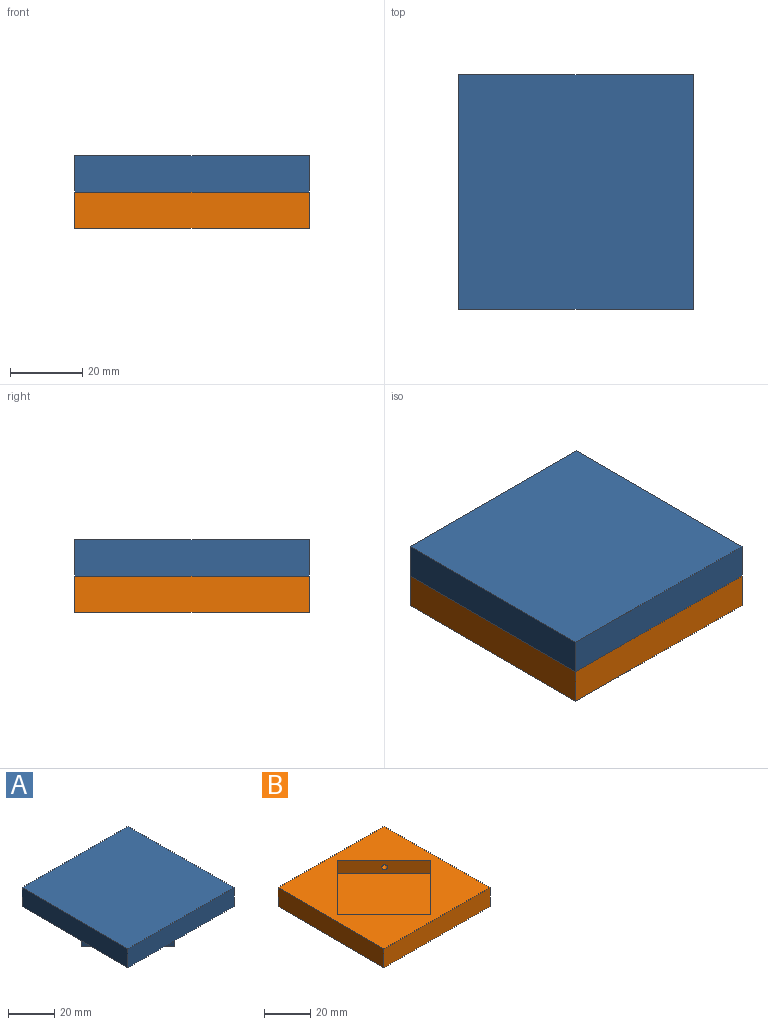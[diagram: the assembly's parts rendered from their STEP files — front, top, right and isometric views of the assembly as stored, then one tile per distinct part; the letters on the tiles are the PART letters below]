
ASSEMBLY  parts=2 mates=1
PART A: 24 faces, bbox 65x65x16.9 mm
  f0: cylinder r=1.25mm len=3.89mm, axis (0.71,0.71,0), area 23.6mm2, adj f1,f15
  f1: plane 2.5x1.77mm, normal (0.71,0.71,0), area 4.9mm2, adj f0
  f2: cylinder r=1.25mm len=3.89mm, axis (-0.71,0.71,0), area 23.6mm2, adj f3,f14
  f3: plane 2.5x1.77mm, normal (-0.71,0.71,0), area 4.9mm2, adj f2
  f4: cylinder r=1.25mm len=3.89mm, axis (-0.71,-0.71,0), area 23.6mm2, adj f5,f13
  f5: plane 2.5x1.77mm, normal (-0.71,-0.71,0), area 4.9mm2, adj f4
  f6: plane 56.57x56.57mm, normal (0,0,-1), area 576mm2, adj f13,f14,f15,f16,f17,f18,f19,f20
  f7: plane 65x10mm, normal (0,1,0), area 650mm2, adj f8,f10,f11,f12
  f8: plane 65x10mm, normal (1,0,0), area 650mm2, adj f7,f9,f11,f12
  f9: plane 65x10mm, normal (0,-1,0), area 650mm2, adj f8,f10,f11,f12
  f10: plane 65x10mm, normal (-1,0,0), area 650mm2, adj f7,f9,f11,f12
  f11: plane 65x65mm, normal (0,0,-1), area 2625mm2, adj f7,f8,f9,f10,f13,f14,f15,f16
  f12: plane 65x65mm, normal (0,0,1), area 4225mm2, adj f7,f8,f9,f10
  f13: plane 28.28x28.28mm, normal (-0.71,-0.71,0), area 271.1mm2, adj f4,f6,f11,f14,f16
  f14: plane 28.28x28.28mm, normal (-0.71,0.71,0), area 271.1mm2, adj f2,f6,f11,f13,f15
  f15: plane 28.28x28.28mm, normal (0.71,0.71,0), area 271.1mm2, adj f0,f6,f11,f14,f16
  f16: plane 28.28x28.28mm, normal (0.71,-0.71,0), area 271.1mm2, adj f6,f11,f13,f15,f22
  f17: plane 22.63x22.63mm, normal (-0.71,0.71,0), area 448mm2, adj f6,f18,f20,f21
  f18: plane 22.63x22.63mm, normal (0.71,0.71,0), area 448mm2, adj f6,f17,f19,f21
  f19: plane 22.63x22.63mm, normal (0.71,-0.71,0), area 448mm2, adj f6,f18,f20,f21
  f20: plane 22.63x22.63mm, normal (-0.71,-0.71,0), area 448mm2, adj f6,f17,f19,f21
  f21: plane 45.26x45.26mm, normal (0,0,-1), area 1024mm2, adj f17,f18,f19,f20
  f22: cylinder r=1.25mm len=3.89mm, axis (0.71,-0.71,0), area 23.6mm2, adj f16,f23
  f23: plane 2.5x1.77mm, normal (0.71,-0.71,0), area 4.9mm2, adj f22
PART B: 19 faces, bbox 65x65x10 mm
  f0: cylinder r=1.25mm len=6.72mm, axis (-0.71,0.71,0), area 55mm2, adj f1,f14
  f1: plane 2.5x1.77mm, normal (-0.71,0.71,0), area 4.9mm2, adj f0
  f2: cylinder r=1.25mm len=6.72mm, axis (-0.71,-0.71,0), area 55mm2, adj f3,f15
  f3: plane 2.5x1.77mm, normal (-0.71,-0.71,0), area 4.9mm2, adj f2
  f4: cylinder r=1.25mm len=6.72mm, axis (0.71,-0.71,0), area 55mm2, adj f5,f12
  f5: plane 2.5x1.77mm, normal (0.71,-0.71,0), area 4.9mm2, adj f4
  f6: plane 65x65mm, normal (0,0,1), area 2576.6mm2, adj f7,f8,f9,f10,f12,f13,f14,f15
  f7: plane 65x10mm, normal (0,1,0), area 650mm2, adj f6,f8,f10,f11
  f8: plane 65x10mm, normal (-1,0,0), area 650mm2, adj f6,f7,f9,f11
  f9: plane 65x10mm, normal (0,-1,0), area 650mm2, adj f6,f8,f10,f11
  f10: plane 65x10mm, normal (1,0,0), area 650mm2, adj f6,f7,f9,f11
  f11: plane 65x65mm, normal (0,0,-1), area 4225mm2, adj f7,f8,f9,f10
  f12: plane 28.71x28.71mm, normal (0.71,-0.71,0), area 279.3mm2, adj f4,f6,f13,f15,f16
  f13: plane 28.71x28.71mm, normal (0.71,0.71,0), area 279.3mm2, adj f6,f12,f14,f16,f17
  f14: plane 28.71x28.71mm, normal (-0.71,0.71,0), area 279.3mm2, adj f0,f6,f13,f15,f16
  f15: plane 28.71x28.71mm, normal (-0.71,-0.71,0), area 279.3mm2, adj f2,f6,f12,f14,f16
  f16: plane 57.42x57.42mm, normal (0,0,1), area 1648.4mm2, adj f12,f13,f14,f15
  f17: cylinder r=1.25mm len=6.72mm, axis (0.71,0.71,0), area 55mm2, adj f13,f18
  f18: plane 2.5x1.77mm, normal (0.71,0.71,0), area 4.9mm2, adj f17
PLACE A t=(3.11,-3.48,0.54)mm
PLACE B t=(3.11,-3.48,-19.46)mm
MATE parallel B.f6 <-> A.f11  axis (0,0,1) through (3.11,-3.48,-9.46)mm
